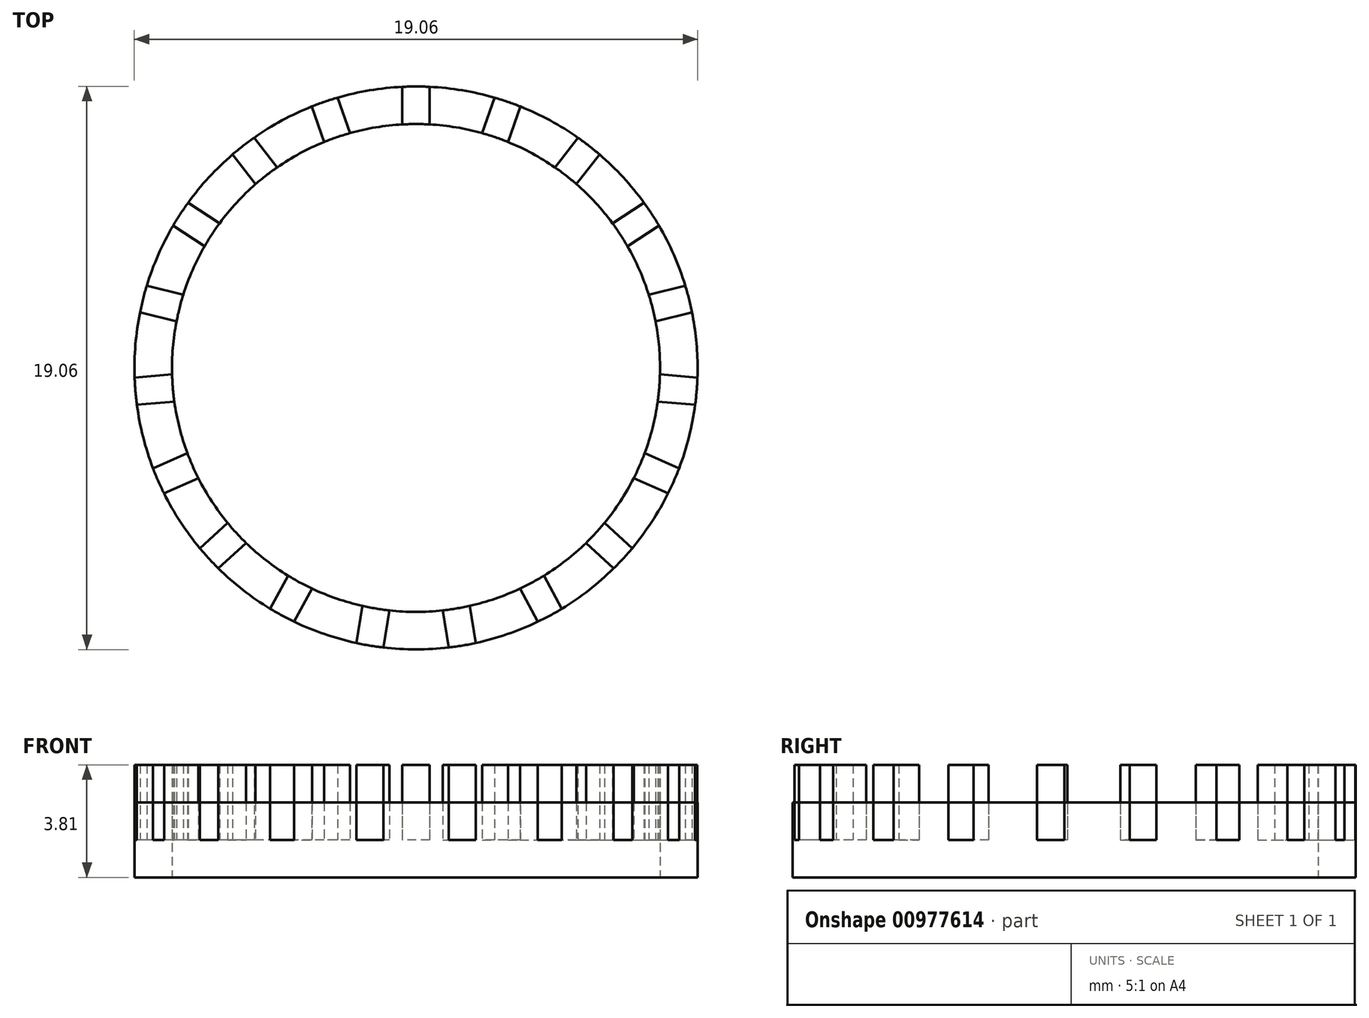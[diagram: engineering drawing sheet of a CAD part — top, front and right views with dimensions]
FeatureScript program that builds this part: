
annotation { "Feature Type Name" : "Feature", "Feature Type Description" : "" }
export const myFeature = defineFeature(function(context is Context, id is Id, definition is map)
    precondition{}
    {
        {
            var Q0;
            Q0=qCreatedBy(makeId("Top.planeOp"),FACE);
            var sketch = newSketch(context, id + "F0", { "sketchPlane" : qUnion([Q0])});
            skCircle(sketch, "E0", {"center": v(0, 0) * mm, "radius": 9.53 * mm});
            skCircle(sketch, "E1", {"center": v(0, 0) * mm, "radius": 8.26 * mm});
            skLineSegment(sketch, "E2.bottom", {"start": v(0.63, 8.87) * mm, "end": v(-0.63, 8.87) * mm});
            skLineSegment(sketch, "E2.top", {"start": v(0.63, 10.18) * mm, "end": v(-0.63, 10.18) * mm});
            skLineSegment(sketch, "E2.left", {"start": v(0.63, 8.87) * mm, "end": v(0.63, 10.18) * mm});
            skLineSegment(sketch, "E2.right", {"start": v(-0.63, 8.87) * mm, "end": v(-0.63, 10.18) * mm});
            skPoint(sketch, "E2.middle", {"position": v(0, 9.53) * mm});
            skPoint(sketch, "E3.middle", {"position": v(0, -9.53) * mm});
            skSolve(sketch);
        }
        {
            var Q0;
            {var subQ0=sQuery(id+"F0.wireOp",EDGE,"E2.left");var subQ1=sQuery(id+"F0.wireOp",EDGE,"E0");var subQ2=makeQuery(id+"F0.imprint","INTERSECT",VERTEX,{"derivedFrom":[subQ1,subQ0]});Q0=makeQuery(id+"F0.imprint","IMPRINT",FACE,{"disambiguationData":[TD([[makeQuery(id+"F0.imprint","IMPRINT",EDGE,{"disambiguationData":[TD([[subQ2,1.0]])],"derivedFrom":subQ1}),1.0]])]});}
            var Q1;
            Q1=makeQuery(id+"F0.imprint","IMPRINT",FACE,{"disambiguationData":[TD([[makeQuery(id+"F0.imprint","IMPRINT",EDGE,{"derivedFrom":sQuery(id+"F0.wireOp",EDGE,"E1")}),-1.0]])]});
            var Q2;
            {var subQ0=sQuery(id+"F0.wireOp",EDGE,"E2.right");var subQ1=sQuery(id+"F0.wireOp",EDGE,"E0");var subQ2=makeQuery(id+"F0.imprint","INTERSECT",VERTEX,{"derivedFrom":[subQ1,subQ0]});Q2=makeQuery(id+"F0.imprint","IMPRINT",FACE,{"disambiguationData":[TD([[makeQuery(id+"F0.imprint","IMPRINT",EDGE,{"disambiguationData":[TD([[subQ2,-1.0]])],"derivedFrom":subQ1}),1.0]])]});}
            var Q3;
            {var subQ5=sQuery(id+"F0.wireOp",EDGE,"E2.bottom");Q3=makeQuery(id+"F0.imprint","IMPRINT",FACE,{"disambiguationData":[TD([[makeQuery(id+"F0.imprint","IMPRINT",EDGE,{"derivedFrom":subQ5}),-1.0]])]});}
            extrude(context, id + "F1", {"entities" : qUnion([Q0, Q1, Q2, Q3]), "depth" : 2.54 * mm, "offsetDistance" : 25.4 * mm});
        }
        {
            var Q0;
            Q0=makeQuery(id+"F1.opExtrude","CAP_FACE",FACE,{"disambiguationData":[OSD([sQuery(id+"F0.wireOp",EDGE,"E0"),sQuery(id+"F0.wireOp",EDGE,"E1")])],"isStart":false});
            var sketch = newSketch(context, id + "F2", { "sketchPlane" : qUnion([Q0])});
            skCircle(sketch, "E4", {"center": v(0, 0) * mm, "radius": 8.9 * mm});
            skLineSegment(sketch, "E5.bottom", {"start": v(0.46, 8.24) * mm, "end": v(-0.46, 8.24) * mm});
            skLineSegment(sketch, "E5.top", {"start": v(0.46, 9.54) * mm, "end": v(-0.46, 9.54) * mm});
            skLineSegment(sketch, "E5.left", {"start": v(0.46, 8.24) * mm, "end": v(0.46, 9.54) * mm});
            skLineSegment(sketch, "E5.right", {"start": v(-0.46, 8.24) * mm, "end": v(-0.46, 9.54) * mm});
            skPoint(sketch, "E5.middle", {"position": v(0, 8.9) * mm});
            skSolve(sketch);
        }
        {
            var Q0;
            Q0=qCreatedBy(makeId("Front.planeOp"),FACE);
            var sketch = newSketch(context, id + "F3", { "sketchPlane" : qUnion([Q0])});
            skLineSegment(sketch, "E6", {"start": v(0, 0) * mm, "end": v(0, 10.34) * mm});
            skSolve(sketch);
        }
        {
            var Q0;
            {var subQ0=sQuery(id+"F2.wireOp",EDGE,"E5.left");var subQ1=sQuery(id+"F2.wireOp",EDGE,"E4");var subQ2=makeQuery(id+"F2.imprint","INTERSECT",VERTEX,{"derivedFrom":[subQ1,subQ0]});Q0=makeQuery(id+"F2.imprint","IMPRINT",FACE,{"disambiguationData":[TD([[makeQuery(id+"F2.imprint","IMPRINT",EDGE,{"disambiguationData":[TD([[subQ2,-1.0]])],"derivedFrom":subQ1}),-1.0]])]});}
            var Q1;
            {var subQ0=sQuery(id+"F2.wireOp",EDGE,"E5.left");var subQ1=sQuery(id+"F2.wireOp",EDGE,"E4");var subQ2=makeQuery(id+"F2.imprint","INTERSECT",VERTEX,{"derivedFrom":[subQ1,subQ0]});Q1=makeQuery(id+"F2.imprint","IMPRINT",FACE,{"disambiguationData":[TD([[makeQuery(id+"F2.imprint","IMPRINT",EDGE,{"disambiguationData":[TD([[subQ2,-1.0]])],"derivedFrom":subQ1}),1.0]])]});}
            extrude(context, id + "F4", {"entities" : qUnion([Q0, Q1]), "endBound" : BoundingType.SYMMETRIC, "depth" : 2.54 * mm, "offsetDistance" : 25.4 * mm});
        }
        {
            var Q0;
            Q0=makeQuery(id+"F4.opExtrude","SWEPT_BODY",BODY,{"disambiguationData":[OSD([sQuery(id+"F0.wireOp",EDGE,"E0"),sQuery(id+"F0.wireOp",EDGE,"E1"),sQuery(id+"F2.wireOp",EDGE,"E5.left"),sQuery(id+"F2.wireOp",EDGE,"E5.right")])]});
            var Q1;
            Q1=sQuery(id+"F3.wireOp",EDGE,"E6");
            circularPattern(context, id + "F5", {"entities" : qUnion([Q0]), "axis" : qUnion([Q1]), "angle" : 360 * degree, "instanceCount" : 19, "equalSpace" : true});
        }
    });
